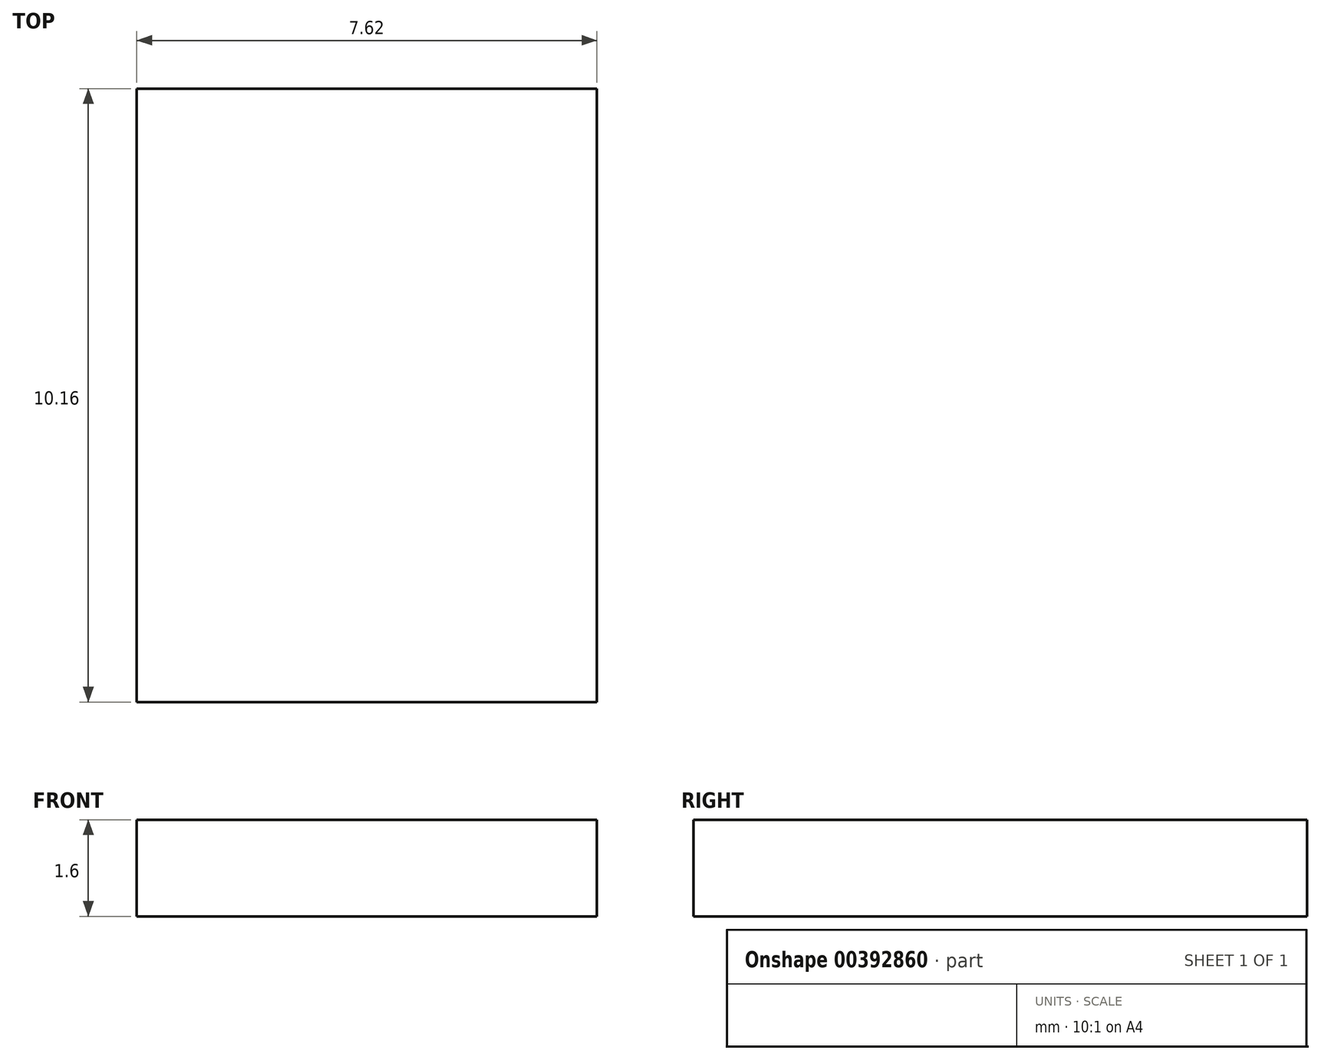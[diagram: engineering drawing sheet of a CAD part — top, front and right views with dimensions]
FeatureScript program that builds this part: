
annotation { "Feature Type Name" : "Feature", "Feature Type Description" : "" }
export const myFeature = defineFeature(function(context is Context, id is Id, definition is map)
    precondition{}
    {
        {
            var Q0;
            Q0=qCreatedBy(makeId("Top.planeOp"),FACE);
            var sketch = newSketch(context, id + "F0", { "sketchPlane" : qUnion([Q0])});
            skLineSegment(sketch, "E0.bottom", {"start": v(3.8, 5.08) * mm, "end": v(-3.81, 5.08) * mm});
            skLineSegment(sketch, "E0.top", {"start": v(3.8, -5.08) * mm, "end": v(-3.81, -5.08) * mm});
            skLineSegment(sketch, "E0.left", {"start": v(3.8, 5.08) * mm, "end": v(3.8, -5.08) * mm});
            skLineSegment(sketch, "E0.right", {"start": v(-3.81, 5.08) * mm, "end": v(-3.81, -5.08) * mm});
            skPoint(sketch, "E0.middle", {"position": v(0, 0) * mm});
            skSolve(sketch);
        }
        {
            var Q0;
            Q0=makeQuery(id+"F0.imprint","IMPRINT",FACE,{"disambiguationData":[TD([[makeQuery(id+"F0.imprint","IMPRINT",EDGE,{"derivedFrom":sQuery(id+"F0.wireOp",EDGE,"E0.bottom")}),1.0]])]});
            extrude(context, id + "F1", {"entities" : qUnion([Q0]), "depth" : 1.6 * mm});
        }
    });
